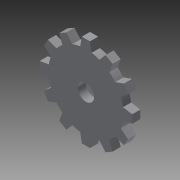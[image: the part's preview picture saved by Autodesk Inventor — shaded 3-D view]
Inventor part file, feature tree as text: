
AUTODESK INVENTOR PART (.ipt)
format: ipt  version: 2013 (Build 170138000, 138)  size: 145,408 bytes
history: native  units: in
note: dims shown in document units (in); Inventor stores cm internally (conversion verified against a paired STEP export)
features: extrude x2, sketch x2
ambient origin geometry x8: Origin, YZ Plane, XZ Plane, XY Plane, X Axis, Y Axis, Z Axis, Center Point
bodies: Solid1 (feature_tree)
feature tree (4):
  extrude  "Extrusion1"  Depth=0.0625in
  extrude  "Extrusion2"  Depth=0.125in
  sketch  "Sketch2"  dims[d1=4.7244in d3=360.0deg d5=0.0625in]
  sketch  "Sketch3"  dims[d8=0.0625in d9=0.0in d10=0.125in d11=0.125in d12=0.0in d13=0.071in d14=0.6871in]
